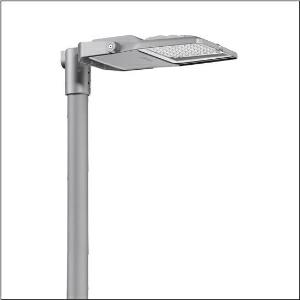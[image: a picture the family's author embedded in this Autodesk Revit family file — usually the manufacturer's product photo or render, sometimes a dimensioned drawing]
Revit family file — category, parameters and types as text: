
# Revit family: floodlight_fl_21_iq_mini___pl43_5xa7771c4a3a_be4f
name_source: partatom
category: Lighting Fixtures
units: mm (PartAtom-declared; Revit-internal decimal feet)

## family parameters
Cut with Voids When Loaded = No
Host = Face
Light Source = No
Part Type = Normal
Room Calculation Point = No
Round Connector Dimension = Use Diameter
Shared = No

## types (1)
- --- (1 x LED, 13050 lm, 87.2 W, 4000K)
    Apparent Load = 87 VA
    CIE Flux Codes = 27 78 99 100 100
    Color Rendering = 70
    Color Temperature = 4000K
    Default Elevation = 1800 mm
    Description = Floodlight FL 21 iQ mini, floodlight, primary light control with lens, of PMMA, primary optical cover: protective disc, of toughened safety glass, transparent, light distribution: PL43, light emission: direct distribution, installation type: surface-mounted, LED, High Power LED, rated luminous flux: 13.050lm, luminous efficacy: 150lm/W, light colour: 740, colour temperature: 4000K, control: Auto-Match, Temp-Guard, Lumen-Switch, Night-Set, Smart-Wire, Light-Fading, Desk-Remote (wireless, voltage-free reading and setting of iQ features in the workshop via application-optimized NFC function/RFID function), optimised constant luminous flux control (CLO 2.0), with terminal, 6-pole, mains connection: 220..240V, AC, 50/60Hz, start of lifetime: 87W, end of service life: 92W, reduction: 40W, luminaire housing, of diecast aluminium, powder-coated, Siteco® metallic grey (DB 702S), corrosivity category C5 mid according to DIN EN ISO 12944, sealing non-destructively replaceable, please order mast flange separately, mast bracket, of steel, galvanised, powder-coated, Siteco® metallic grey (DB 702S), protection rating (complete): IP66, insulation class (complete): insulation class II (safety insulation), certification: CE, ENEC, VDE, protection symbol: D, impact resistance: IK08, permissible operating ambient temperature: -40..+40°C, permissible operating ambient temperature for outdoor applications: -40..+50°C, standard: DIN EN 12944, LABS conformity tested according to VDMA 24364:2018-05, packaging unit: 1 piece

Light Distribution: PL43
    Height = 70 mm
    Lamp = 1 x LED
    Lamp Light Flux = 13050 lm
    Lamp Power = 87.2 W
    Lamp count = 1
    Length = 485 mm
    Luminous efficacy = 150 lm/W
    Manufacturer = Siteco
    ModVariant = No
    Model = 5XA7771C4A3A
    Number of Poles = 1
    OnlyDefault = Yes
    Power Factor = 1
    Product Name = Floodlight FL 21 iQ mini | PL43
    Product group = floodlight | pylon annexe
    ProductGroupID = 6200
    Protection Class = Protection class II
    Protection Degree = IP 66
    RLX_Detail_Level = 1
    RLX_Emergency_Light_Flux = 0 lm
    RLX_Emergency_Type = 0
    RLX_Emergency_Type_DB = No
    RlxData = <blob elided: 101285 chars, md5=357243c3>
    Socket = socket
    Standby Power = 0 W
    System Light Flux = 13050 lm
    System Power = 87 W
    Type Comments = factory setting: luminous flux: 100 % | dim-lin: 254 | 456 mA
    Type Image = l_1007125.jpg
    URL = http://relux.com
    VarID = @adj_132763
    Voltage = 0 V
    Weight = 0.00 kg
    Width = 337 mm

## geometry (parser evidence)
native form markers: Blend x4, Sweep x13
no freeform markers — native parametric forms only
